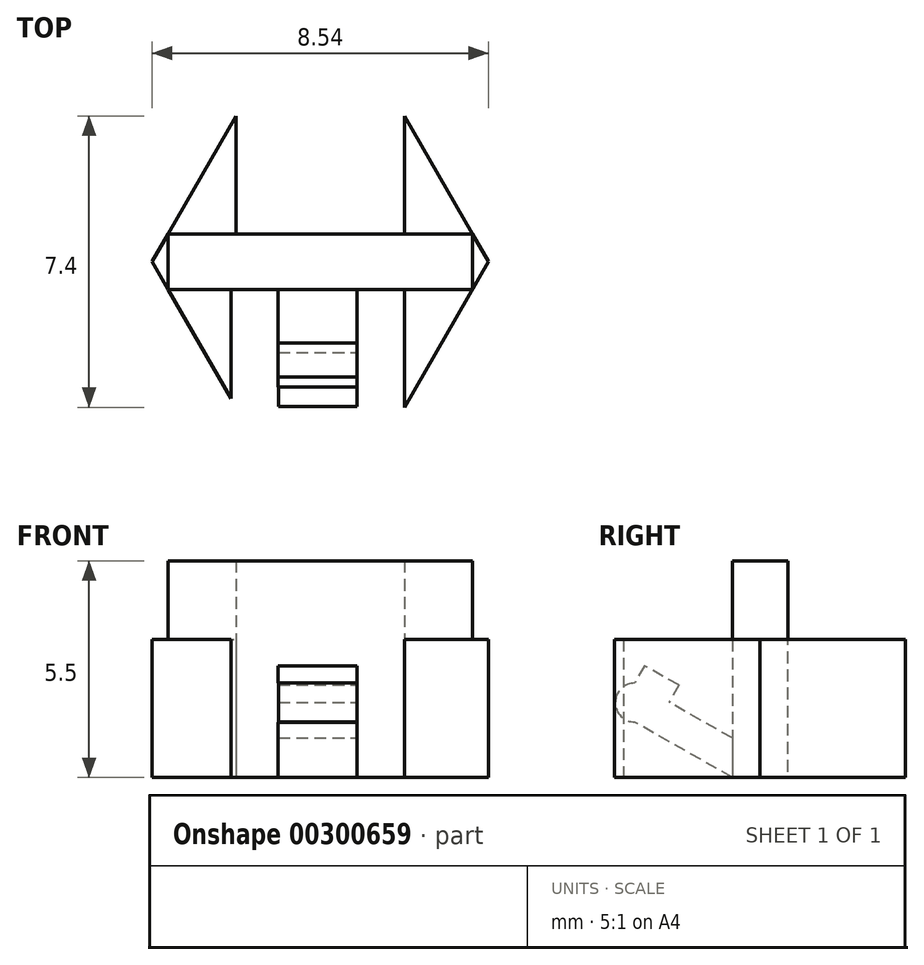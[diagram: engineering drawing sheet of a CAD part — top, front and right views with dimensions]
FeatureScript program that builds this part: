
annotation { "Feature Type Name" : "Feature", "Feature Type Description" : "" }
export const myFeature = defineFeature(function(context is Context, id is Id, definition is map)
    precondition{}
    {
        {
            var Q0;
            Q0=qCreatedBy(makeId("Top.planeOp"),FACE);
            var sketch = newSketch(context, id + "F0", { "sketchPlane" : qUnion([Q0])});
            skCircle(sketch, "E0.cCircle", {"center": v(0, 0) * mm, "radius": 3.7 * mm, "construction": true});
            skLineSegment(sketch, "E0.0", {"start": v(4.27, 0) * mm, "end": v(2.14, -3.7) * mm});
            skLineSegment(sketch, "E0.2", {"start": v(-2.14, -3.7) * mm, "end": v(-4.27, 0) * mm});
            skLineSegment(sketch, "E0.3", {"start": v(-4.27, 0) * mm, "end": v(-2.14, 3.7) * mm});
            skLineSegment(sketch, "E0.4", {"start": v(-2.14, 3.7) * mm, "end": v(2.14, 3.7) * mm});
            skLineSegment(sketch, "E0.5", {"start": v(2.14, 3.7) * mm, "end": v(4.27, 0) * mm});
            skPoint(sketch, "E0.0.midPoint", {"position": v(3.2, -1.85) * mm});
            skLineSegment(sketch, "E1.left", {"start": v(-2.14, 3.7) * mm, "end": v(-2.14, 3.7) * mm});
            skLineSegment(sketch, "E1.right", {"start": v(2.14, 3.7) * mm, "end": v(2.14, 3.7) * mm});
            skLineSegment(sketch, "E2.bottom", {"start": v(2.14, 3.7) * mm, "end": v(-2.14, 3.7) * mm});
            skLineSegment(sketch, "E2.top", {"start": v(2.14, 0.7) * mm, "end": v(-2.14, 0.7) * mm});
            skLineSegment(sketch, "E2.left", {"start": v(2.14, 3.7) * mm, "end": v(2.14, 0.7) * mm});
            skLineSegment(sketch, "E2.right", {"start": v(-2.14, 3.7) * mm, "end": v(-2.14, 0.7) * mm});
            skLineSegment(sketch, "E3.left", {"start": v(2.14, -3.7) * mm, "end": v(2.14, -3.7) * mm});
            skLineSegment(sketch, "E3.right", {"start": v(-2.14, -3.7) * mm, "end": v(-2.14, -3.7) * mm});
            skLineSegment(sketch, "E4", {"start": v(-2.14, -3.7) * mm, "end": v(2.14, -3.7) * mm});
            skLineSegment(sketch, "E5.bottom", {"start": v(2.14, -3.7) * mm, "end": v(-2.27, -3.7) * mm});
            skLineSegment(sketch, "E5.top", {"start": v(2.14, -0.7) * mm, "end": v(-2.27, -0.7) * mm});
            skLineSegment(sketch, "E5.left", {"start": v(2.14, -3.7) * mm, "end": v(2.14, -0.7) * mm});
            skLineSegment(sketch, "E5.right", {"start": v(-2.27, -3.7) * mm, "end": v(-2.27, -0.7) * mm});
            skSolve(sketch);
        }
        {
            var Q0;
            Q0=makeQuery(id+"F0.imprint","IMPRINT",FACE,{"disambiguationData":[TD([[makeQuery(id+"F0.imprint","IMPRINT",EDGE,{"derivedFrom":sQuery(id+"F0.wireOp",EDGE,"E0.0")}),-1.0]])]});
            extrude(context, id + "F1", {"entities" : qUnion([Q0]), "depth" : 3.5 * mm});
        }
        {
            var Q0;
            Q0=makeQuery(id+"F1.opExtrude","SWEPT_FACE",FACE,{"disambiguationData":[OSD([sQuery(id+"F0.wireOp",EDGE,"E5.top")])]});
            var sketch = newSketch(context, id + "F2", { "sketchPlane" : qUnion([Q0])});
            skLineSegment(sketch, "E6.top", {"start": v(-2.21, 0) * mm, "end": v(2.14, 0) * mm});
            skPoint(sketch, "E7", {"position": v(-2.21, 0.5) * mm});
            skLineSegment(sketch, "E8.bottom", {"start": v(-1.07, 1) * mm, "end": v(0.94, 1) * mm});
            skLineSegment(sketch, "E8.top", {"start": v(-1.07, 0) * mm, "end": v(0.94, 0) * mm});
            skLineSegment(sketch, "E8.left", {"start": v(-1.07, 1) * mm, "end": v(-1.07, 0) * mm});
            skLineSegment(sketch, "E8.right", {"start": v(0.94, 1) * mm, "end": v(0.94, 0) * mm});
            skSolve(sketch);
        }
        {
            var Q0;
            Q0=makeQuery(id+"F1.opExtrude","SWEPT_FACE",FACE,{"disambiguationData":[OSD([sQuery(id+"F0.wireOp",EDGE,"E5.right")])]});
            var sketch = newSketch(context, id + "F3", { "sketchPlane" : qUnion([Q0])});
            skLineSegment(sketch, "E9", {"start": v(-0.7, 0) * mm, "end": v(-3.18, 1.4) * mm});
            skSolve(sketch);
        }
        {
            var Q0;
            Q0=makeQuery(id+"F2.imprint","IMPRINT",FACE,{"disambiguationData":[TD([[makeQuery(id+"F2.imprint","IMPRINT",EDGE,{"derivedFrom":sQuery(id+"F2.wireOp",EDGE,"E6.bottom")}),-1.0]])]});
            var Q1;
            Q1=makeQuery(id+"F2.imprint","IMPRINT",FACE,{"disambiguationData":[TD([[makeQuery(id+"F2.imprint","IMPRINT",EDGE,{"derivedFrom":sQuery(id+"F2.wireOp",EDGE,"E8.bottom")}),-1.0]])]});
            var Q2;
            Q2=sQuery(id+"F3.wireOp",EDGE,"E9");
            sweep(context, id + "F4", {"operationType" : NewBodyOperationType.ADD, "profiles" : qUnion([Q0, Q1]), "path" : qUnion([Q2])});
        }
        {
            var Q0;
            Q0=makeQuery(id+"F4.opSweep","SWEPT_FACE",FACE,{"disambiguationData":[OSD([sQuery(id+"F2.wireOp",EDGE,"E8.bottom"),sQuery(id+"F3.wireOp",EDGE,"GSqznCnj-m1VF-RyfH-3CS4-RMuIAuQ8SG67")])]});
            var sketch = newSketch(context, id + "F5", { "sketchPlane" : qUnion([Q0])});
            skLineSegment(sketch, "E10.bottom", {"start": v(-1.07, -3.95) * mm, "end": v(0.94, -3.95) * mm});
            skLineSegment(sketch, "E10.top", {"start": v(-1.07, -2.95) * mm, "end": v(0.94, -2.95) * mm});
            skLineSegment(sketch, "E10.left", {"start": v(-1.07, -3.95) * mm, "end": v(-1.07, -2.95) * mm});
            skLineSegment(sketch, "E10.right", {"start": v(0.94, -3.95) * mm, "end": v(0.94, -2.95) * mm});
            skSolve(sketch);
        }
        {
            var Q0;
            Q0=makeQuery(id+"F5.imprint","IMPRINT",FACE,{"disambiguationData":[TD([[makeQuery(id+"F5.imprint","IMPRINT",EDGE,{"derivedFrom":sQuery(id+"F5.wireOp",EDGE,"E10.bottom")}),-1.0]])]});
            extrude(context, id + "F6", {"entities" : qUnion([Q0]), "operationType" : NewBodyOperationType.ADD, "depth" : 0.5 * mm});
        }
        {
            var Q0;
            Q0=makeQuery(id+"F6.boolean.opBoolean","MERGE",FACE,{"derivedFrom":[makeQuery(id+"F4.opSweep","SWEPT_FACE",FACE,{"disambiguationData":[OSD([sQuery(id+"F2.wireOp",EDGE,"E8.right"),sQuery(id+"F3.wireOp",EDGE,"E9")])]}),makeQuery(id+"F6.opExtrude","SWEPT_FACE",FACE,{"disambiguationData":[OSD([sQuery(id+"F5.wireOp",EDGE,"E10.right")])]})]});
            var sketch = newSketch(context, id + "F7", { "sketchPlane" : qUnion([Q0])});
            skCircle(sketch, "E11", {"center": v(-3.18, 1.9) * mm, "radius": 0.5 * mm});
            skSolve(sketch);
        }
        {
            var Q0;
            {var subQ0=sQuery(id+"F7.wireOp",EDGE,"E11");var subQ1=makeQuery(id+"F4.opSweep","CAP_EDGE",EDGE,{"disambiguationData":[OSD([sQuery(id+"F2.wireOp",EDGE,"E8.right"),sQuery(id+"F3.wireOp",VERTEX,"E9.end")])],"isStart":false});var subQ2=makeQuery(id+"F7.imprint","INTERSECT",VERTEX,{"disambiguationData":[OD(0.0)],"derivedFrom":[subQ1,subQ0]});Q0=makeQuery(id+"F7.imprint","IMPRINT",FACE,{"disambiguationData":[TD([[makeQuery(id+"F7.imprint","IMPRINT",EDGE,{"disambiguationData":[TD([[subQ2,1.0]])],"derivedFrom":subQ0}),1.0]])]});}
            extrude(context, id + "F8", {"entities" : qUnion([Q0]), "operationType" : NewBodyOperationType.ADD, "oppositeDirection" : true, "depth" : 2 * mm});
        }
        {
            var Q0;
            Q0=makeQuery(id+"F1.opExtrude","CAP_FACE",FACE,{"disambiguationData":[OSD([sQuery(id+"F0.wireOp",EDGE,"E0.0"),sQuery(id+"F0.wireOp",EDGE,"E0.2"),sQuery(id+"F0.wireOp",EDGE,"E0.3"),sQuery(id+"F0.wireOp",EDGE,"E0.5"),sQuery(id+"F0.wireOp",EDGE,"E2.top"),sQuery(id+"F0.wireOp",EDGE,"E2.left"),sQuery(id+"F0.wireOp",EDGE,"E2.right"),sQuery(id+"F0.wireOp",EDGE,"E5.top"),sQuery(id+"F0.wireOp",EDGE,"E5.left"),sQuery(id+"F0.wireOp",EDGE,"E5.right")])],"isStart":false});
            var sketch = newSketch(context, id + "F9", { "sketchPlane" : qUnion([Q0])});
            skLineSegment(sketch, "E12.bottom", {"start": v(-3.87, -0.7) * mm, "end": v(3.86, -0.7) * mm});
            skLineSegment(sketch, "E12.top", {"start": v(-3.87, 0.7) * mm, "end": v(3.86, 0.7) * mm});
            skLineSegment(sketch, "E12.left", {"start": v(-3.87, -0.7) * mm, "end": v(-3.87, 0.7) * mm});
            skLineSegment(sketch, "E12.right", {"start": v(3.86, -0.7) * mm, "end": v(3.86, 0.7) * mm});
            skSolve(sketch);
        }
        {
            var Q0;
            {var subQ0=sQuery(id+"F9.wireOp",EDGE,"E12.right");Q0=makeQuery(id+"F9.imprint","IMPRINT",FACE,{"disambiguationData":[TD([[makeQuery(id+"F9.imprint","IMPRINT",EDGE,{"derivedFrom":subQ0}),1.0]])]});}
            extrude(context, id + "F10", {"entities" : qUnion([Q0]), "operationType" : NewBodyOperationType.ADD, "depth" : 2 * mm});
        }
    });
